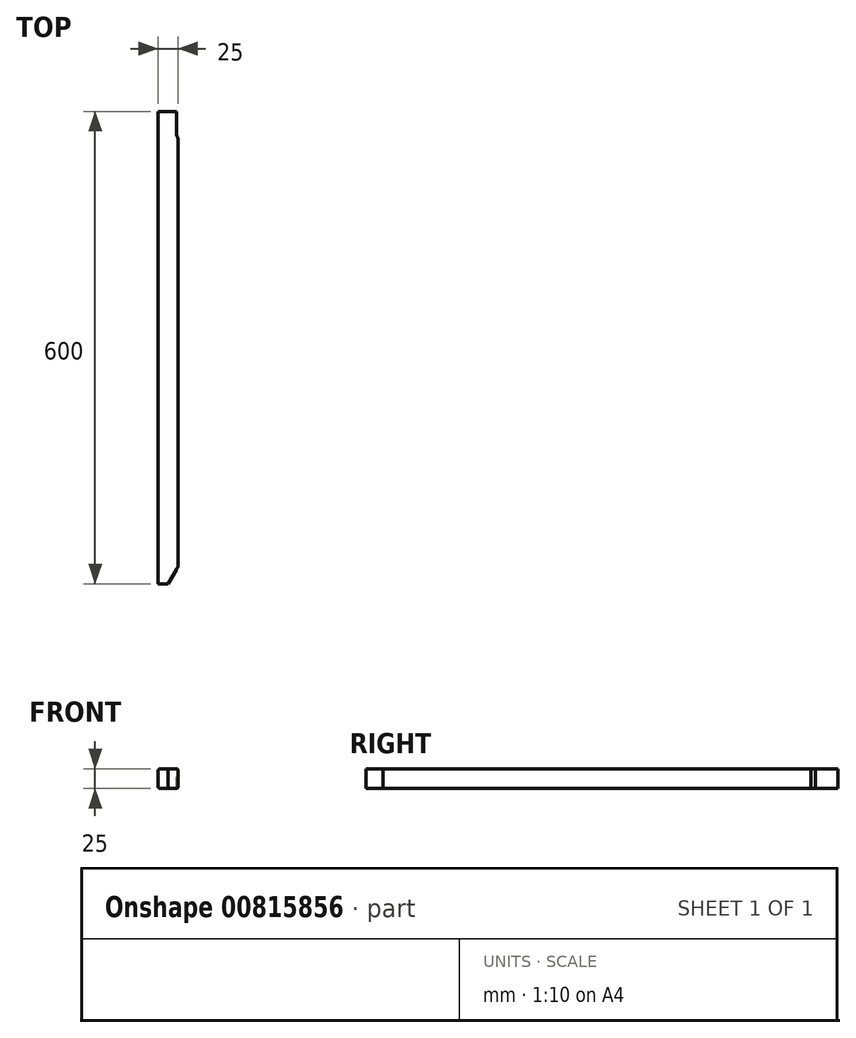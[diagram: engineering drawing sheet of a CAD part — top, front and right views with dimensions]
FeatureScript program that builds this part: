
annotation { "Feature Type Name" : "Feature", "Feature Type Description" : "" }
export const myFeature = defineFeature(function(context is Context, id is Id, definition is map)
    precondition{}
    {
        {
            var Q0;
            Q0=qCreatedBy(makeId("Front.planeOp"),FACE);
            var sketch = newSketch(context, id + "F0", { "sketchPlane" : qUnion([Q0])});
            skLineSegment(sketch, "E0.bottom", {"start": v(10.5, 12.5) * mm, "end": v(-10.5, 12.5) * mm});
            skLineSegment(sketch, "E0.top", {"start": v(10.5, -12.5) * mm, "end": v(-10.5, -12.5) * mm});
            skLineSegment(sketch, "E0.left", {"start": v(12.5, 10.5) * mm, "end": v(12.5, -10.5) * mm});
            skLineSegment(sketch, "E0.right", {"start": v(-12.5, 10.5) * mm, "end": v(-12.5, -10.5) * mm});
            skPoint(sketch, "E0.middle", {"position": v(0, 0) * mm});
            skPoint(sketch, "E1.visualSharp", {"position": v(12.5, 12.5) * mm});
            skArc(sketch, "E1.filletArc", {"start": v(12.5, 10.5) * mm, "mid": v(11.91, 11.91) * mm, "end": v(10.5, 12.5) * mm});
            skPoint(sketch, "E2.visualSharp", {"position": v(-12.5, 12.5) * mm});
            skArc(sketch, "E2.filletArc", {"start": v(-10.5, 12.5) * mm, "mid": v(-11.91, 11.91) * mm, "end": v(-12.5, 10.5) * mm});
            skPoint(sketch, "E3.visualSharp", {"position": v(-12.5, -12.5) * mm});
            skArc(sketch, "E3.filletArc", {"start": v(-12.5, -10.5) * mm, "mid": v(-11.91, -11.91) * mm, "end": v(-10.5, -12.5) * mm});
            skPoint(sketch, "E4.visualSharp", {"position": v(12.5, -12.5) * mm});
            skArc(sketch, "E4.filletArc", {"start": v(10.5, -12.5) * mm, "mid": v(11.91, -11.91) * mm, "end": v(12.5, -10.5) * mm});
            skSolve(sketch);
        }
        {
            var Q0;
            Q0 = qSketchRegion(id + "F0", true);
            extrude(context, id + "F1", {"entities" : qUnion([Q0]), "depth" : 600 * mm, "offsetDistance" : 25 * mm});
        }
        {
            var Q0;
            Q0=makeQuery(id+"F1.opExtrude","SWEPT_FACE",FACE,{"disambiguationData":[OSD([sQuery(id+"F0.wireOp",EDGE,"E0.bottom")])]});
            var sketch = newSketch(context, id + "F2", { "sketchPlane" : qUnion([Q0])});
            skLineSegment(sketch, "E5", {"start": v(12.5, 0) * mm, "end": v(12.5, -34.34) * mm});
            skLineSegment(sketch, "E6", {"start": v(0, 0) * mm, "end": v(12.5, -34.34) * mm});
            skLineSegment(sketch, "E7", {"start": v(0, 0) * mm, "end": v(12.5, 0) * mm});
            skLineSegment(sketch, "E8", {"start": v(12.5, -578.35) * mm, "end": v(0, -600) * mm});
            skLineSegment(sketch, "E9", {"start": v(0, -600) * mm, "end": v(12.5, -600) * mm});
            skLineSegment(sketch, "E10", {"start": v(12.5, -600) * mm, "end": v(12.5, -578.35) * mm});
            skSolve(sketch);
        }
        {
            var Q0;
            {var subQ0=sQuery(id+"F2.wireOp",EDGE,"E5");Q0=makeQuery(id+"F2.imprint","IMPRINT",FACE,{"disambiguationData":[TD([[makeQuery(id+"F2.imprint","IMPRINT",EDGE,{"derivedFrom":subQ0}),-1.0]])]});}
            var Q1;
            {var subQ0=sQuery(id+"F2.wireOp",EDGE,"E10");Q1=makeQuery(id+"F2.imprint","IMPRINT",FACE,{"disambiguationData":[TD([[makeQuery(id+"F2.imprint","IMPRINT",EDGE,{"derivedFrom":subQ0}),1.0]])]});}
            var Q2;
            {var subQ0=sQuery(id+"F2.wireOp",EDGE,"E7");var subQ1=sQuery(id+"F2.wireOp",EDGE,"E6");var subQ2=sQuery(id+"F0.wireOp",EDGE,"E0.bottom");var subQ3=makeQuery(id+"F2.imprint","INTERSECT",VERTEX,{"derivedFrom":[makeQuery(id+"F1.opExtrude","CAP_EDGE",EDGE,{"disambiguationData":[OSD([subQ2])],"isStart":true}),subQ1,subQ0]});Q2=makeQuery(id+"F2.imprint","IMPRINT",FACE,{"disambiguationData":[TD([[makeQuery(id+"F2.imprint","IMPRINT",EDGE,{"disambiguationData":[TD([[subQ3,1.0]])],"derivedFrom":subQ1}),-1.0]])]});}
            var Q3;
            {var subQ0=sQuery(id+"F2.wireOp",EDGE,"E9");var subQ1=sQuery(id+"F2.wireOp",EDGE,"E8");var subQ2=sQuery(id+"F0.wireOp",EDGE,"E0.bottom");var subQ3=makeQuery(id+"F2.imprint","INTERSECT",VERTEX,{"derivedFrom":[makeQuery(id+"F1.opExtrude","CAP_EDGE",EDGE,{"disambiguationData":[OSD([subQ2])],"isStart":false}),subQ1,subQ0]});Q3=makeQuery(id+"F2.imprint","IMPRINT",FACE,{"disambiguationData":[TD([[makeQuery(id+"F2.imprint","IMPRINT",EDGE,{"disambiguationData":[TD([[subQ3,1.0]])],"derivedFrom":subQ1}),1.0]])]});}
            extrude(context, id + "F3", {"entities" : qUnion([Q0, Q1, Q2, Q3]), "operationType" : NewBodyOperationType.REMOVE, "endBound" : BoundingType.THROUGH_ALL, "oppositeDirection" : true, "depth" : 25 * mm, "offsetDistance" : 25 * mm});
        }
    });
